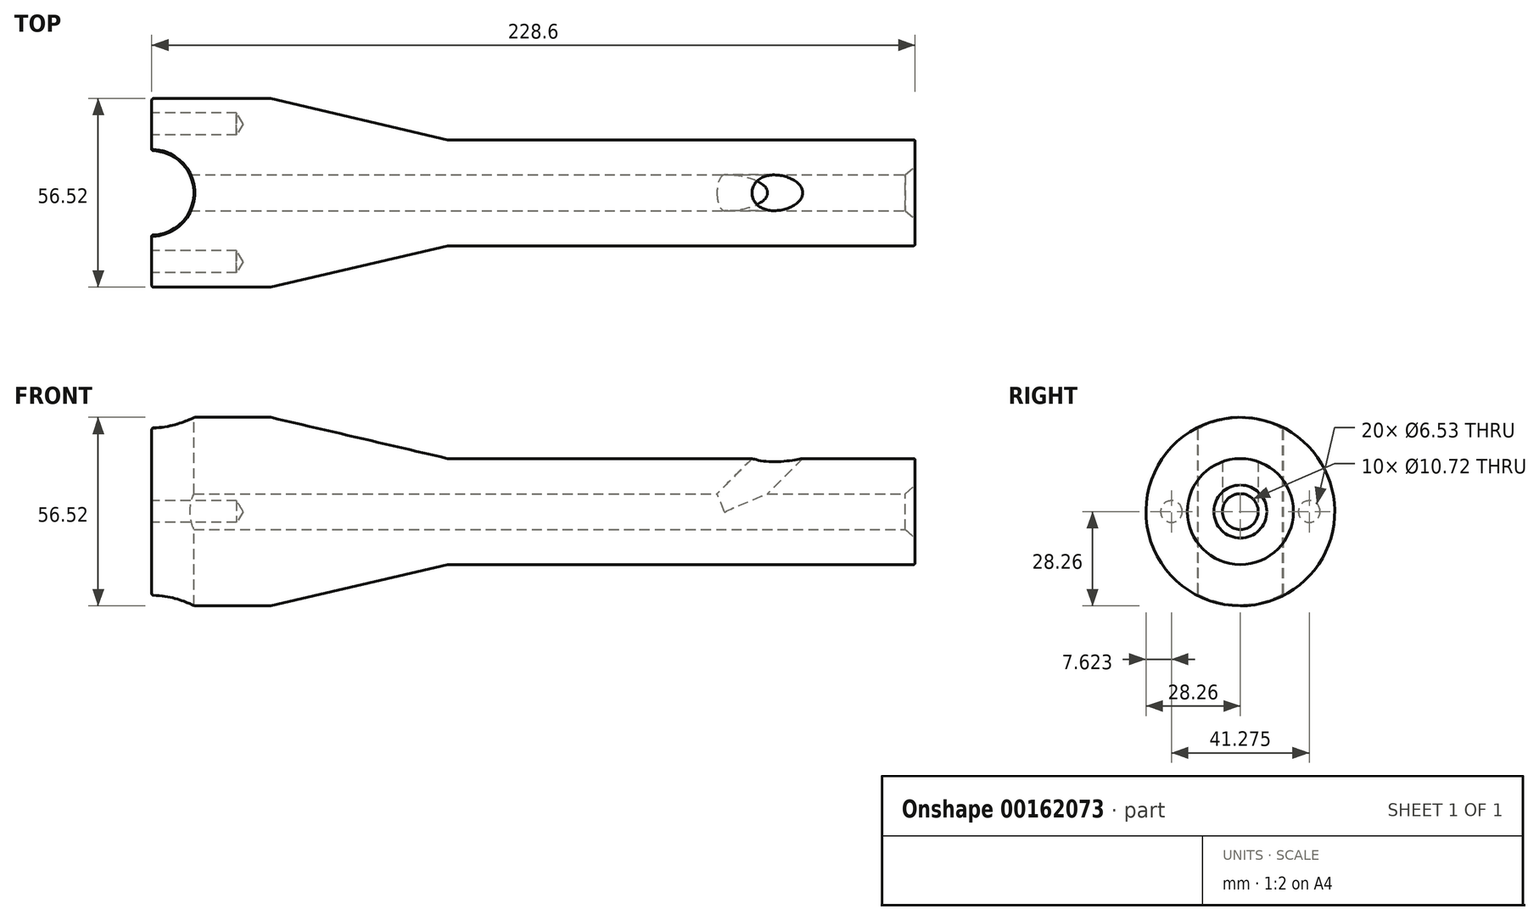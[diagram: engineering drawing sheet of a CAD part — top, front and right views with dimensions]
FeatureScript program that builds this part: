
annotation { "Feature Type Name" : "Feature", "Feature Type Description" : "" }
export const myFeature = defineFeature(function(context is Context, id is Id, definition is map)
    precondition{}
    {
        {
            var Q0;
            Q0=qCreatedBy(makeId("Front.planeOp"),FACE);
            var sketch = newSketch(context, id + "F0", { "sketchPlane" : qUnion([Q0])});
            skLineSegment(sketch, "E0", {"start": v(0, 0) * mm, "end": v(0, 28.26) * mm});
            skLineSegment(sketch, "E1", {"start": v(0, 28.26) * mm, "end": v(35.56, 28.26) * mm});
            skLineSegment(sketch, "E2", {"start": v(35.56, 28.26) * mm, "end": v(88.65, 15.87) * mm});
            skLineSegment(sketch, "E3", {"start": v(88.65, 15.87) * mm, "end": v(228.6, 15.87) * mm});
            skLineSegment(sketch, "E4", {"start": v(228.6, 15.87) * mm, "end": v(228.6, 0) * mm});
            skLineSegment(sketch, "E5", {"start": v(0, 0) * mm, "end": v(228.6, 0) * mm});
            skSolve(sketch);
        }
        {
            var Q0;
            Q0=qSketchRegion(id+"F0",true);
            var Q1;
            Q1=sQuery(id+"F0.wireOp",EDGE,"E5");
            revolve(context, id + "F1", {"entities" : qUnion([Q0]), "axis" : qUnion([Q1]), "revolveType" : RevolveType.FULL});
        }
        {
            var Q0;
            Q0=makeQuery(id+"F1.opRevolve","SWEPT_FACE",FACE,{"disambiguationData":[OSD([sQuery(id+"F0.wireOp",EDGE,"E4")])]});
            var sketch = newSketch(context, id + "F2", { "sketchPlane" : qUnion([Q0])});
            skPoint(sketch, "E6", {"position": v(0, 0) * mm});
            skSolve(sketch);
        }
        {
            var Q0;
            Q0=sQuery(id+"F2.wireOp",VERTEX,"E6");
            var Q1;
            Q1=makeQuery(id+"F1.opRevolve","SWEPT_BODY",BODY,{"disambiguationData":[OSD([sQuery(id+"F0.wireOp",EDGE,"E0"),sQuery(id+"F0.wireOp",EDGE,"E1"),sQuery(id+"F0.wireOp",EDGE,"E2"),sQuery(id+"F0.wireOp",EDGE,"E3"),sQuery(id+"F0.wireOp",EDGE,"E4"),sQuery(id+"F0.wireOp",EDGE,"E5")])]});
            hole(context, id + "F3", {"style" : HoleStyle.C_SINK, "endStyle" : HoleEndStyle.BLIND, "holeDiameter" : 10.72 * mm, "cSinkDiameter" : 15.88 * mm, "cSinkAngle" : 82 * degree, "holeDepth" : 38.1 * mm, "locations" : qUnion([Q0]), "scope" : qUnion([Q1])});
        }
        {
            var Q0;
            Q0=makeQuery(id+"F1.opRevolve","SWEPT_FACE",FACE,{"disambiguationData":[OSD([sQuery(id+"F0.wireOp",EDGE,"E0")])]});
            var sketch = newSketch(context, id + "F4", { "sketchPlane" : qUnion([Q0])});
            skPoint(sketch, "E7", {"position": v(0, 0) * mm});
            skSolve(sketch);
        }
        {
            var Q0;
            Q0=sQuery(id+"F4.wireOp",VERTEX,"E7");
            var Q1;
            Q1=makeQuery(id+"F1.opRevolve","SWEPT_BODY",BODY,{"disambiguationData":[OSD([sQuery(id+"F0.wireOp",EDGE,"E0"),sQuery(id+"F0.wireOp",EDGE,"E1"),sQuery(id+"F0.wireOp",EDGE,"E2"),sQuery(id+"F0.wireOp",EDGE,"E3"),sQuery(id+"F0.wireOp",EDGE,"E4"),sQuery(id+"F0.wireOp",EDGE,"E5")])]});
            hole(context, id + "F5", {"style" : HoleStyle.SIMPLE, "endStyle" : HoleEndStyle.BLIND, "holeDiameter" : 10.72 * mm, "holeDepth" : 191 * mm, "locations" : qUnion([Q0]), "scope" : qUnion([Q1])});
        }
        {
            var Q0;
            Q0=makeQuery(id+"F1.opRevolve","SWEPT_EDGE",EDGE,{"disambiguationData":[OSD([sQuery(id+"F0.wireOp",EDGE,"E0"),sQuery(id+"F0.wireOp",EDGE,"E1")])]});
            var Q1;
            Q1=makeQuery(id+"F1.opRevolve","SWEPT_EDGE",EDGE,{"disambiguationData":[OSD([sQuery(id+"F0.wireOp",EDGE,"E1"),sQuery(id+"F0.wireOp",EDGE,"E2")])]});
            var Q2;
            Q2=makeQuery(id+"F1.opRevolve","SWEPT_EDGE",EDGE,{"disambiguationData":[OSD([sQuery(id+"F0.wireOp",EDGE,"E2"),sQuery(id+"F0.wireOp",EDGE,"E3")])]});
            var Q3;
            Q3=makeQuery(id+"F1.opRevolve","SWEPT_EDGE",EDGE,{"disambiguationData":[OSD([sQuery(id+"F0.wireOp",EDGE,"E3"),sQuery(id+"F0.wireOp",EDGE,"E4")])]});
            fillet(context, id + "F6", {"entities" : qUnion([Q0, Q1, Q2, Q3]), "radius" : 0.5 * mm, "tangentPropagation" : true, "allowEdgeOverflow" : false});
        }
        {
            var Q0;
            Q0=qCreatedBy(makeId("Top.planeOp"),FACE);
            var sketch = newSketch(context, id + "F7", { "sketchPlane" : qUnion([Q0])});
            skPoint(sketch, "E8", {"position": v(0, 0) * mm});
            skCircle(sketch, "E9", {"center": v(0, 0) * mm, "radius": 12.64 * mm});
            skSolve(sketch);
        }
        {
            var Q0;
            Q0=makeQuery(id+"F7.imprint","IMPRINT",FACE,{"disambiguationData":[TD([[makeQuery(id+"F7.imprint","IMPRINT",EDGE,{"derivedFrom":sQuery(id+"F7.wireOp",EDGE,"E9")}),1.0]])]});
            extrude(context, id + "F8", {"entities" : qUnion([Q0]), "operationType" : NewBodyOperationType.REMOVE, "endBound" : BoundingType.THROUGH_ALL, "oppositeDirection" : true, "depth" : 25.4 * mm, "hasSecondDirection" : true, "secondDirectionBound" : SecondDirectionBoundingType.THROUGH_ALL, "secondDirectionOppositeDirection" : false, "secondDirectionDepth" : 25.4 * mm});
        }
        {
            var Q0;
            Q0=qCreatedBy(makeId("Top.planeOp"),FACE);
            var sketch = newSketch(context, id + "F9", { "sketchPlane" : qUnion([Q0])});
            skLineSegment(sketch, "E10", {"start": v(171.45, 61.21) * mm, "end": v(171.45, -62.5) * mm});
            skSolve(sketch);
        }
        {
            var Q0;
            Q0=sQuery(id+"F9.wireOp",EDGE,"E10");
            cPlane(context, id + "F10", {"entities" : qUnion([Q0]), "cplaneType" : CPlaneType.LINE_ANGLE, "offset" : 25.4 * mm, "angle" : 135 * degree, "width" : 152.4 * mm, "height" : 152.4 * mm});
        }
        {
            var Q0;
            Q0=qCreatedBy(id+"F10.planeOp",FACE);
            var sketch = newSketch(context, id + "F11", { "sketchPlane" : qUnion([Q0])});
            skCircle(sketch, "E11", {"center": v(0, -121.25) * mm, "radius": 5.36 * mm});
            skSolve(sketch);
        }
        {
            var Q0;
            Q0 = qSketchRegion(id + "F11", true);
            extrude(context, id + "F12", {"entities" : qUnion([Q0]), "operationType" : NewBodyOperationType.REMOVE, "depth" : 32.77 * mm});
        }
        {
            var Q0;
            Q0=makeQuery(id+"F8.boolean.opBoolean","SPLIT",FACE,{"disambiguationData":[OD(1.0)],"derivedFrom":makeQuery(id+"F1.opRevolve","SWEPT_FACE",FACE,{"disambiguationData":[OSD([sQuery(id+"F0.wireOp",EDGE,"E0")])]})});
            var sketch = newSketch(context, id + "F13", { "sketchPlane" : qUnion([Q0])});
            skLineSegment(sketch, "E12", {"start": v(-27.75, 0) * mm, "end": v(27.72, 0) * mm});
            skPoint(sketch, "E13", {"position": v(-20.64, 0) * mm});
            skPoint(sketch, "E14", {"position": v(20.64, 0) * mm});
            skSolve(sketch);
        }
        {
            var Q0;
            Q0=sQuery(id+"F13.wireOp",VERTEX,"E13");
            var Q1;
            Q1=sQuery(id+"F13.wireOp",VERTEX,"E14");
            var Q2;
            Q2=makeQuery(id+"F1.opRevolve","SWEPT_BODY",BODY,{"disambiguationData":[OSD([sQuery(id+"F0.wireOp",EDGE,"E0"),sQuery(id+"F0.wireOp",EDGE,"E1"),sQuery(id+"F0.wireOp",EDGE,"E2"),sQuery(id+"F0.wireOp",EDGE,"E3"),sQuery(id+"F0.wireOp",EDGE,"E4"),sQuery(id+"F0.wireOp",EDGE,"E5")])]});
            hole(context, id + "F14", {"style" : HoleStyle.SIMPLE, "endStyle" : HoleEndStyle.BLIND, "standardTappedOrClearance" : lookupTablePath({ "standard" : "ANSI", "engagement" : "75%", "pitch" : "18 tpi", "size" : "5/16", "type" : "Tapped" }), "standardBlindInLast" : lookupTablePath({ "standard" : "ANSI", "engagement" : "75%", "pitch" : "18 tpi", "size" : "5/16", "type" : "Tapped" }), "holeDiameter" : 6.53 * mm, "holeDepth" : 25.4 * mm, "locations" : qUnion([Q0, Q1]), "scope" : qUnion([Q2]), "majorDiameter" : 7.94 * mm});
        }
        {
            var Q0;
            Q0=makeQuery(id+"F8.boolean.opBoolean","INTERSECT",EDGE,{"disambiguationData":[OD(1.0)],"derivedFrom":[makeQuery(id+"F1.opRevolve","SWEPT_FACE",FACE,{"disambiguationData":[OSD([sQuery(id+"F0.wireOp",EDGE,"E1")])]}),makeQuery(id+"F8.opExtrude","SWEPT_FACE",FACE,{"disambiguationData":[OSD([sQuery(id+"F7.wireOp",EDGE,"E9")])]})]});
            var Q1;
            Q1=makeQuery(id+"F8.boolean.opBoolean","INTERSECT",EDGE,{"disambiguationData":[OD(0.0)],"derivedFrom":[makeQuery(id+"F1.opRevolve","SWEPT_FACE",FACE,{"disambiguationData":[OSD([sQuery(id+"F0.wireOp",EDGE,"E1")])]}),makeQuery(id+"F8.opExtrude","SWEPT_FACE",FACE,{"disambiguationData":[OSD([sQuery(id+"F7.wireOp",EDGE,"E9")])]})]});
            chamfer(context, id + "F15", {"entities" : qUnion([Q0, Q1]), "width" : 0.25 * mm, "tangentPropagation" : true});
        }
    });
